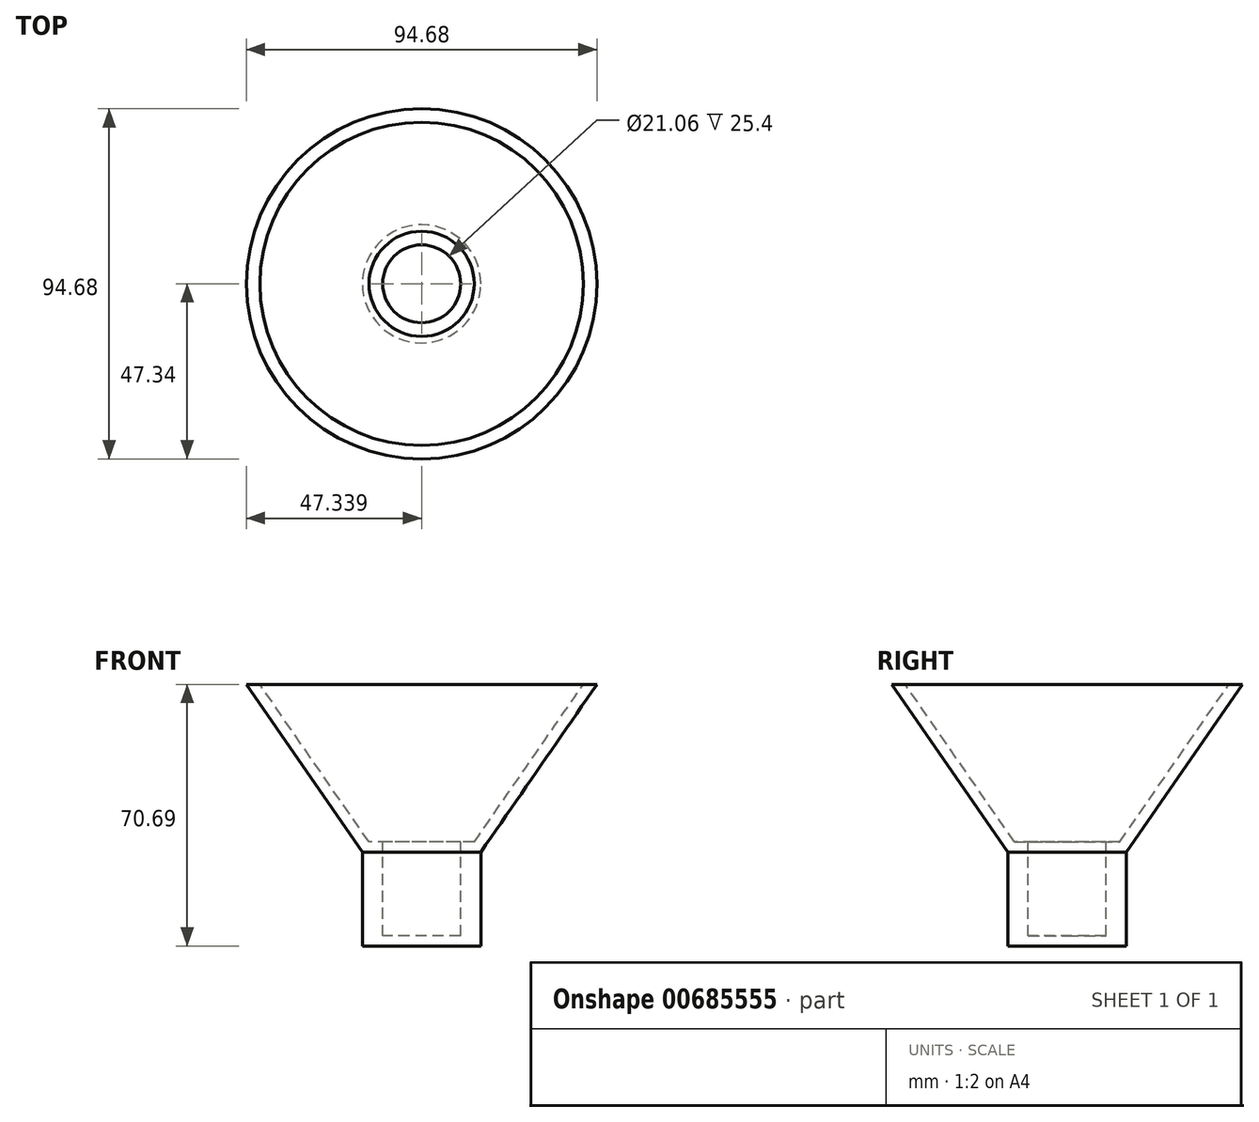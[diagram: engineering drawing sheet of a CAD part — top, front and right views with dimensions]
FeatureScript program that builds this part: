
annotation { "Feature Type Name" : "Feature", "Feature Type Description" : "" }
export const myFeature = defineFeature(function(context is Context, id is Id, definition is map)
    precondition{}
    {
        {
            var Q0;
            Q0=qCreatedBy(makeId("Front.planeOp"),FACE);
            var sketch = newSketch(context, id + "F0", { "sketchPlane" : qUnion([Q0])});
            skPoint(sketch, "E0.start.orphan", {"position": v(1.72, 0) * mm});
            skLineSegment(sketch, "E1", {"start": v(0, 0) * mm, "end": v(1.72, 0) * mm});
            skLineSegment(sketch, "E2", {"start": v(25.4, 0) * mm, "end": v(25.4, 25.4) * mm});
            skLineSegment(sketch, "E3", {"start": v(25.4, 25.4) * mm, "end": v(56.75, 70.7) * mm});
            skLineSegment(sketch, "E4", {"start": v(56.75, 70.7) * mm, "end": v(53.1, 70.7) * mm});
            skLineSegment(sketch, "E5", {"start": v(53.1, 70.7) * mm, "end": v(23.63, 28.1) * mm});
            skLineSegment(sketch, "E6", {"start": v(23.63, 28.1) * mm, "end": v(9.4, 28.1) * mm});
            skLineSegment(sketch, "E7", {"start": v(9.4, 28.1) * mm, "end": v(9.4, 0) * mm});
            skPoint(sketch, "E7.endSnap0", {"position": v(12.7, 0) * mm});
            skLineSegment(sketch, "E8.trimOffspring", {"start": v(9.4, 0) * mm, "end": v(25.4, 0) * mm});
            skSolve(sketch);
        }
        {
            var Q0;
            Q0=makeQuery(id+"F0.imprint","IMPRINT",FACE,{"disambiguationData":[TD([[makeQuery(id+"F0.imprint","IMPRINT",EDGE,{"derivedFrom":sQuery(id+"F0.wireOp",EDGE,"E2")}),1.0]])]});
            var Q1;
            Q1=sQuery(id+"F0.wireOp",EDGE,"E7");
            revolve(context, id + "F1", {"entities" : qUnion([Q0]), "axis" : qUnion([Q1]), "revolveType" : RevolveType.FULL});
        }
        {
            var Q0;
            Q0=makeQuery(id+"F1.opRevolve","SWEPT_FACE",FACE,{"disambiguationData":[OSD([sQuery(id+"F0.wireOp",EDGE,"E6")])]});
            var sketch = newSketch(context, id + "F2", { "sketchPlane" : qUnion([Q0])});
            skCircle(sketch, "E9", {"center": v(9.4, 0) * mm, "radius": 10.53 * mm});
            skSolve(sketch);
        }
        {
            var Q0;
            Q0 = qSketchRegion(id + "F2", true);
            extrude(context, id + "F3", {"entities" : qUnion([Q0]), "operationType" : NewBodyOperationType.REMOVE, "oppositeDirection" : true, "depth" : 25.4 * mm, "offsetDistance" : 25.4 * mm});
        }
    });
